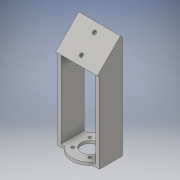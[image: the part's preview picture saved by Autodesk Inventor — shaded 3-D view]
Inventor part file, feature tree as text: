
AUTODESK INVENTOR PART (.ipt)
format: ipt  version: 2016 (Build 200138000, 138)  size: 170,496 bytes
history: native  units: in
note: dims shown in document units (in); Inventor stores cm internally (conversion verified against a paired STEP export)
features: sketch x7, extrude x5, hole x2, chamfer x1
ambient origin geometry x8: Origin, YZ Plane, XZ Plane, XY Plane, X Axis, Y Axis, Z Axis, Center Point
bodies: Solid1 (feature_tree)
feature tree (15):
  extrude  "Extrusion1"  Depth=0.1575in TaperAngle=0.0deg
  extrude  "Extrusion2"  Depth=0.7874in
  extrude  "Extrusion3"  Depth=0.1969in
  extrude  "Extrusion4"  Depth=5.6693in
  hole  "Hole1"  [1 undecoded]
  chamfer  "Chamfer1"  Distance=1.5748in Angle=360.0deg
  extrude  "Extrusion5"  Depth=1.3081in TaperAngle=45.0deg
  hole  "Hole2"  [1 undecoded]
  sketch  "Sketch1"  dims[d0=2.0472in d4=0.1575in d5=0.0in]
  sketch  "Sketch2"  dims[d6=2.0472in d7=1.811in d8=0.7874in]
  sketch  "Sketch3"  dims[d10=0.1575in d11=0.0in d12=0.1969in]
  sketch  "Sketch4"  dims[d13=5.6693in d14=0.0in d15=0.9843in]
  sketch  "Sketch5"  dims[d16=0.9843in d17=0.1575in d18=0.0in]
  sketch  "Sketch6"  dims[d19=0.4872in]
  sketch  "Sketch7"  dims[d20=0.4872in d21=1.5748in d23=360.0deg d25=0.1772in d26=0.75in d27=0.375in d28=0.25in d29=0.5635in d30=1.0in d31=0.8108in d32=1.3081in d33=0.125in d34=45.0deg d35=0.1575in d36=0.0in d37=2.3622in d38=1.1811in d39=0.4in d40=0.4in d41=0.1969in d42=0.75in d43=0.375in d44=0.25in d45=0.5635in d46=1.0in d47=0.8108in]
note: 2 required parameter values undecoded (feature->parameter linkage not recoverable at this tier; creation-order binding heuristic only, values carry confidence <= 0.55)
